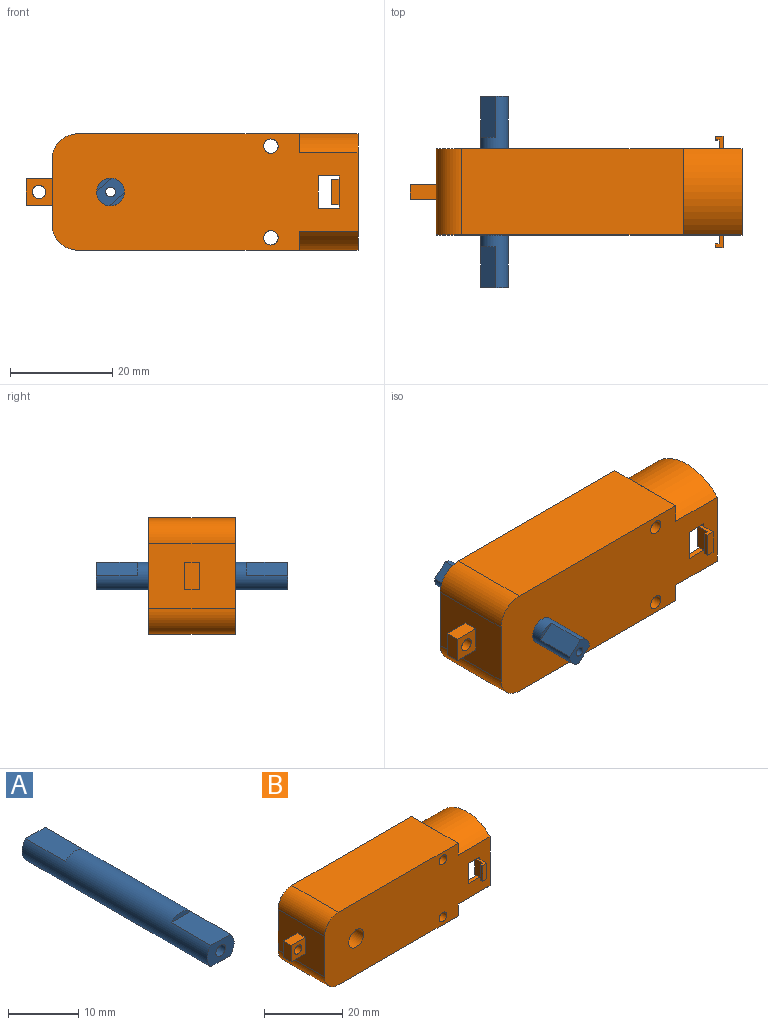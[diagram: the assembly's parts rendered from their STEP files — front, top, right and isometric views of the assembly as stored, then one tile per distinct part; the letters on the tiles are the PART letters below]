
ASSEMBLY  parts=2 mates=1
PART A: 12 faces, bbox 5.4x37.3x5.4 mm
  f0: plane 5.4x3.7mm, normal (0,1,0), area 15.4mm2, adj f2,f7,f8,f10
  f1: plane 5.4x3.7mm, normal (0,-1,0), area 15.4mm2, adj f2,f3,f5,f7
  f2: cylinder r=2.7mm len=37.3mm, axis (0,1,0), area 491.8mm2, adj f0,f1,f3,f4,f5,f6,f8,f9
  f3: plane 8x3.93mm, normal (0,0,-1), area 31.5mm2, adj f1,f2,f4
  f4: plane 3.93x0.85mm, normal (0,-1,0), area 2.3mm2, adj f2,f3
  f5: plane 8x3.93mm, normal (0,0,1), area 31.5mm2, adj f1,f2,f6
  f6: plane 3.93x0.85mm, normal (0,-1,0), area 2.3mm2, adj f2,f5
  f7: cylinder r=0.95mm len=37.3mm, axis (0,-1,0), area 222.6mm2, adj f0,f1
  f8: plane 8x3.93mm, normal (0,0,-1), area 31.5mm2, adj f0,f2,f9
  f9: plane 3.93x0.85mm, normal (0,1,0), area 2.3mm2, adj f2,f8
  f10: plane 8x3.93mm, normal (0,0,1), area 31.5mm2, adj f0,f2,f11
  f11: plane 3.93x0.85mm, normal (0,1,0), area 2.3mm2, adj f2,f10
PART B: 66 faces, bbox 64.8x21.8x22.7 mm
  f0: plane 4.9x2.85mm, normal (-1,0,0), area 14mm2, adj f33,f55,f56,f64
  f1: plane 59.7x22.7mm, normal (0,1,0), area 1197.9mm2, adj f20,f21,f22,f24,f25,f26,f27,f28
  f2: plane 4.9x2.85mm, normal (-1,0,0), area 14mm2, adj f4,f44,f46,f53
  f3: plane 59.7x22.7mm, normal (0,-1,0), area 1197.9mm2, adj f19,f22,f23,f24,f25,f26,f27,f28
  f4: plane 14.39x11.5mm, normal (0,1,0), area 143.3mm2, adj f2,f32,f34,f36,f37,f44,f46,f48
  f5: plane 14.6x2.26mm, normal (0,0,-1), area 33.1mm2, adj f8,f10,f14,f15
  f6: plane 14.6x2.26mm, normal (0,0,1), area 33.1mm2, adj f8,f13,f14,f15
  f7: plane 35.56x14.6mm, normal (0,0,1), area 519.2mm2, adj f13,f14,f15,f17
  f8: plane 20.5x14.6mm, normal (-1,0,0), area 275.5mm2, adj f5,f6,f14,f15,f18
  f9: plane 35.56x14.6mm, normal (0,0,-1), area 519.2mm2, adj f10,f14,f15,f16
  f10: cylinder r=2.5mm len=14.6mm, axis (0,1,0), area 154.6mm2, adj f5,f9,f14,f15
  f11: cylinder r=3.8mm len=14.6mm, axis (0,1,0), area 348.6mm2, adj f14,f15
  f12: plane 14.6x12.7mm, normal (1,0,0), area 185.4mm2, adj f14,f15,f16,f17
  f13: cylinder r=2.5mm len=14.6mm, axis (0,1,0), area 154.6mm2, adj f6,f7,f14,f15
  f14: plane 46x20.5mm, normal (0,1,0), area 859.1mm2, adj f5,f6,f7,f8,f9,f10,f11,f12
  f15: plane 46x20.5mm, normal (0,-1,0), area 859.1mm2, adj f5,f6,f7,f8,f9,f10,f11,f12
  f16: cylinder r=3.9mm len=14.6mm, axis (0,1,0), area 89.4mm2, adj f9,f12,f14,f15
  f17: cylinder r=3.9mm len=14.6mm, axis (0,-1,0), area 89.4mm2, adj f7,f12,f14,f15
  f18: cylinder r=2.75mm len=5.5mm, axis (1,0,0), area 19mm2, adj f8,f37
  f19: plane 8.4x3.72mm, normal (1,0,0), area 9.6mm2, adj f3,f22,f35
  f20: plane 8.4x3.72mm, normal (1,0,0), area 9.6mm2, adj f1,f22,f35
  f21: plane 8.4x3.72mm, normal (1,0,0), area 9.6mm2, adj f1,f24,f31
  f22: plane 43.2x16.8mm, normal (0,0,-1), area 725.8mm2, adj f1,f3,f19,f20,f30
  f23: plane 8.4x3.72mm, normal (1,0,0), area 9.6mm2, adj f3,f24,f31
  f24: plane 43.2x16.8mm, normal (0,0,1), area 725.8mm2, adj f1,f3,f21,f23,f29
  f25: cylinder r=1.4mm len=16.8mm, axis (0,1,0), area 147.8mm2, adj f1,f3
  f26: cylinder r=2.7mm len=16.8mm, axis (0,1,0), area 285mm2, adj f1,f3
  f27: plane 16.8x12.7mm, normal (-1,0,0), area 199.1mm2, adj f1,f3,f29,f30,f38,f39,f40,f41
  f28: cylinder r=1.4mm len=16.8mm, axis (0,1,0), area 147.8mm2, adj f1,f3
  f29: cylinder r=5mm len=16.8mm, axis (0,1,0), area 131.9mm2, adj f1,f3,f24,f27
  f30: cylinder r=5mm len=16.8mm, axis (0,-1,0), area 131.9mm2, adj f1,f3,f22,f27
  f31: cylinder r=11.35mm len=16.8mm, axis (-1,0,0), area 217.5mm2, adj f1,f3,f21,f23,f36
  f32: cylinder r=10.25mm len=14.6mm, axis (-1,0,0), area 186.9mm2, adj f4,f33,f36,f37
  f33: plane 14.39x11.5mm, normal (0,-1,0), area 143.3mm2, adj f0,f32,f34,f36,f37,f55,f56,f59
  f34: cylinder r=10.25mm len=14.6mm, axis (-1,0,0), area 186.9mm2, adj f4,f33,f36,f37
  f35: cylinder r=11.35mm len=16.8mm, axis (-1,0,0), area 217.5mm2, adj f1,f3,f19,f20,f36
  f36: plane 22.7x16.8mm, normal (1,0,0), area 71.3mm2, adj f1,f3,f4,f31,f32,f33,f34,f35
  f37: plane 20.5x14.6mm, normal (1,0,0), area 247.8mm2, adj f4,f18,f32,f33,f34
  f38: plane 5.1x2.8mm, normal (0,0,-1), area 14.3mm2, adj f27,f39,f41,f42
  f39: plane 5.1x5.1mm, normal (0,-1,0), area 20.7mm2, adj f27,f38,f40,f42,f43
  f40: plane 5.1x2.8mm, normal (0,0,1), area 14.3mm2, adj f27,f39,f41,f42
  f41: plane 5.1x5.1mm, normal (0,1,0), area 20.7mm2, adj f27,f38,f40,f42,f43
  f42: plane 5.1x2.8mm, normal (-1,0,0), area 14.3mm2, adj f38,f39,f40,f41
  f43: cylinder r=1.3mm len=2.8mm, axis (0,-1,0), area 22.9mm2, adj f39,f41
  f44: plane 3.6x1.5mm, normal (0,0,-1), area 3.3mm2, adj f2,f4,f45,f47,f52,f53,f54
  f45: plane 4.9x2.5mm, normal (1,0,0), area 12.2mm2, adj f3,f44,f46,f47
  f46: plane 3.6x1.5mm, normal (0,0,1), area 3.3mm2, adj f2,f4,f45,f47,f48,f53,f54
  f47: plane 4.9x1.5mm, normal (0,-1,0), area 7.4mm2, adj f44,f45,f46,f54
  f48: plane 1.1x0.7mm, normal (-1,0,0), area 0.8mm2, adj f3,f4,f46,f49
  f49: plane 4.1x1.1mm, normal (0,0,-1), area 4.5mm2, adj f3,f4,f48,f50
  f50: plane 6.3x1.1mm, normal (1,0,0), area 6.9mm2, adj f3,f4,f49,f51
  f51: plane 4.1x1.1mm, normal (0,0,1), area 4.5mm2, adj f3,f4,f50,f52
  f52: plane 1.1x0.7mm, normal (-1,0,0), area 0.8mm2, adj f3,f4,f44,f51
  f53: plane 4.9x0.75mm, normal (0,1,0), area 3.7mm2, adj f2,f44,f46,f54
  f54: plane 4.9x0.75mm, normal (-1,0,0), area 3.7mm2, adj f44,f46,f47,f53
  f55: plane 3.6x1.5mm, normal (0,0,-1), area 3.3mm2, adj f0,f33,f57,f58,f59,f64,f65
  f56: plane 3.6x1.5mm, normal (0,0,1), area 3.3mm2, adj f0,f33,f57,f58,f63,f64,f65
  f57: plane 4.9x2.5mm, normal (1,0,0), area 12.2mm2, adj f1,f55,f56,f58
  f58: plane 4.9x1.5mm, normal (0,1,0), area 7.4mm2, adj f55,f56,f57,f65
  f59: plane 1.1x0.7mm, normal (-1,0,0), area 0.8mm2, adj f1,f33,f55,f60
  f60: plane 4.1x1.1mm, normal (0,0,1), area 4.5mm2, adj f1,f33,f59,f61
  f61: plane 6.3x1.1mm, normal (1,0,0), area 6.9mm2, adj f1,f33,f60,f62
  f62: plane 4.1x1.1mm, normal (0,0,-1), area 4.5mm2, adj f1,f33,f61,f63
  f63: plane 1.1x0.7mm, normal (-1,0,0), area 0.8mm2, adj f1,f33,f56,f62
  f64: plane 4.9x0.75mm, normal (0,-1,0), area 3.7mm2, adj f0,f55,f56,f65
  f65: plane 4.9x0.75mm, normal (-1,0,0), area 3.7mm2, adj f55,f56,f58,f64
PLACE A rot(axis=(0,-1,0),40.8deg) t=(-5.05,2.07,10.29)mm
PLACE B t=(-1.97,2.07,1.99)mm fixed
MATE revolute A.f2 <-> B.f11  axis (0,1,0) through (-14.67,2.07,1.99)mm
